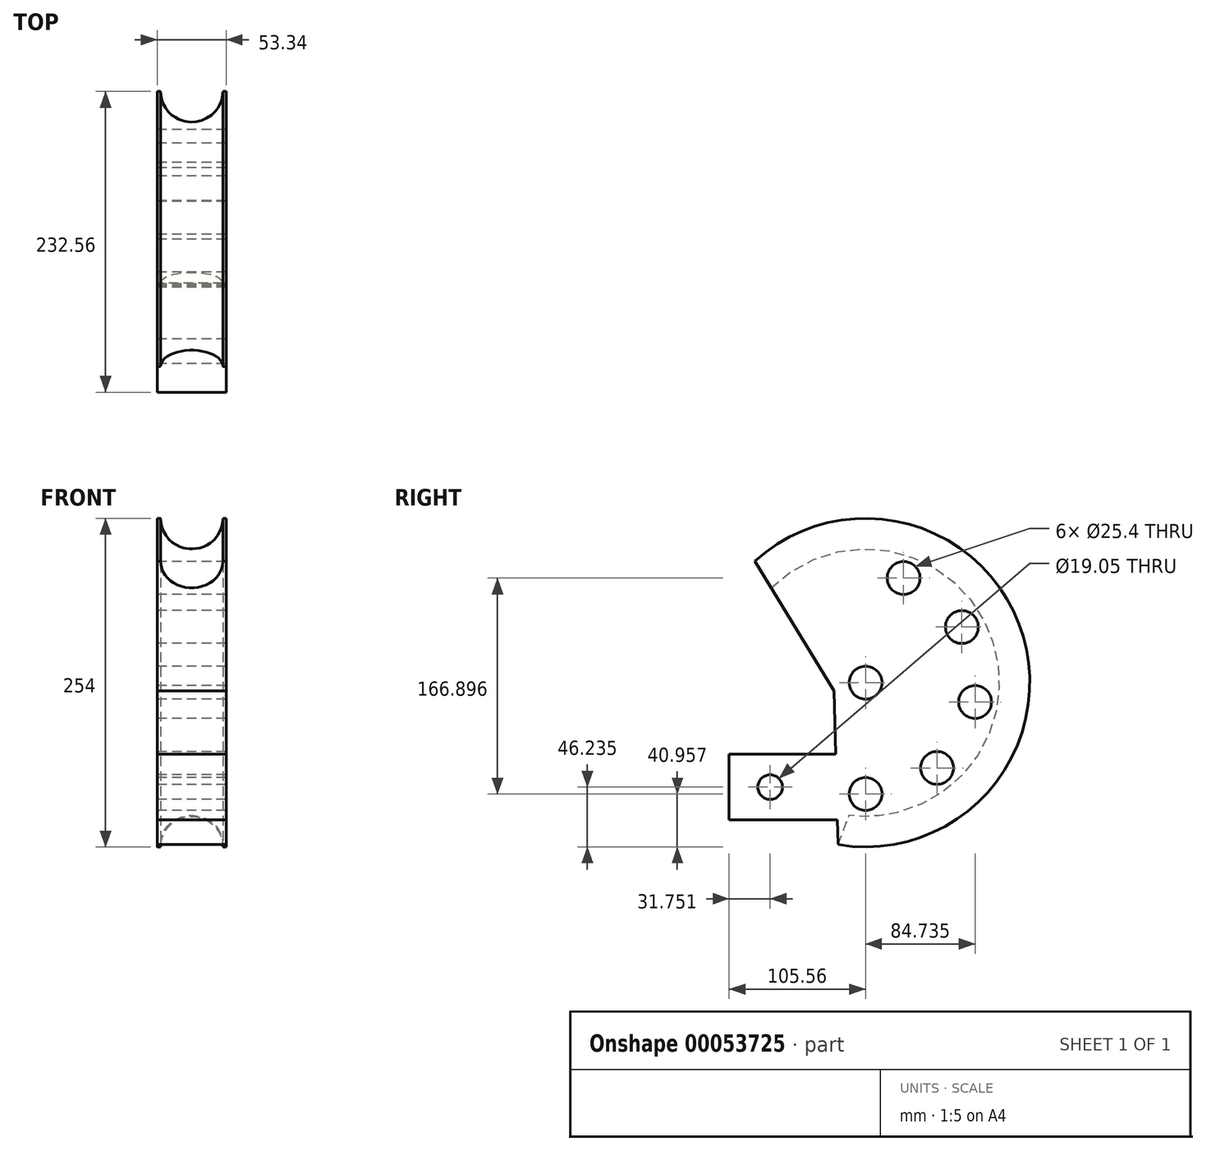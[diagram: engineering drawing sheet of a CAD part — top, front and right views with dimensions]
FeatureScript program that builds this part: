
annotation { "Feature Type Name" : "Feature", "Feature Type Description" : "" }
export const myFeature = defineFeature(function(context is Context, id is Id, definition is map)
    precondition{}
    {
        {
            var Q0;
            Q0=qCreatedBy(makeId("Right.planeOp"),FACE);
            var sketch = newSketch(context, id + "F0", { "sketchPlane" : qUnion([Q0])});
            skArc(sketch, "E0", {"start": v(-21.25, -125.2) * mm, "mid": v(121.85, 35.79) * mm, "end": v(-85.58, 93.83) * mm});
            skCircle(sketch, "E1", {"center": v(0, 0) * mm, "radius": 12.7 * mm});
            skCircle(sketch, "E2", {"center": v(0, -86.04) * mm, "radius": 12.7 * mm});
            skCircle(sketch, "E3.1.0", {"center": v(55.3, -65.91) * mm, "radius": 12.7 * mm});
            skCircle(sketch, "E3.2.0", {"center": v(84.74, -14.94) * mm, "radius": 12.7 * mm});
            skLineSegment(sketch, "E3.anchor1", {"start": v(0, 0) * mm, "end": v(0, -86.04) * mm, "construction": true});
            skLineSegment(sketch, "E3.anchor2", {"start": v(0, 0) * mm, "end": v(29.43, 80.85) * mm, "construction": true});
            skCircle(sketch, "E4.1.3.0", {"center": v(74.51, 43.02) * mm, "radius": 12.7 * mm});
            skCircle(sketch, "E4.1.4.0", {"center": v(29.43, 80.85) * mm, "radius": 12.7 * mm});
            skLineSegment(sketch, "E5.0", {"start": v(-24.24, -6.5) * mm, "end": v(-23, -55.37) * mm});
            skLineSegment(sketch, "E5.1", {"start": v(-24.24, -6.5) * mm, "end": v(-85.58, 93.83) * mm});
            skLineSegment(sketch, "E6", {"start": v(-21.73, -106.17) * mm, "end": v(-105.56, -106.17) * mm});
            skLineSegment(sketch, "E7", {"start": v(-105.56, -106.17) * mm, "end": v(-105.56, -55.37) * mm});
            skLineSegment(sketch, "E8", {"start": v(-105.56, -55.37) * mm, "end": v(-23, -55.37) * mm});
            skLineSegment(sketch, "E9.trimOffspring", {"start": v(-21.73, -106.17) * mm, "end": v(-21.25, -125.2) * mm});
            skCircle(sketch, "E10", {"center": v(-73.8, -80.77) * mm, "radius": 9.53 * mm});
            skPoint(sketch, "E10.centerSnap0", {"position": v(-105.56, -80.77) * mm});
            skSolve(sketch);
        }
        {
            var Q0;
            Q0=makeQuery(id+"F0.imprint","IMPRINT",FACE,{"disambiguationData":[TD([[makeQuery(id+"F0.imprint","IMPRINT",EDGE,{"derivedFrom":sQuery(id+"F0.wireOp",EDGE,"E0")}),1.0]])]});
            extrude(context, id + "F1", {"entities" : qUnion([Q0]), "depth" : 53.34 * mm});
        }
        {
            var Q0;
            Q0=makeQuery(id+"F1.opExtrude","SWEPT_FACE",FACE,{"disambiguationData":[OSD([sQuery(id+"F0.wireOp",EDGE,"E5.1")])]});
            var sketch = newSketch(context, id + "F2", { "sketchPlane" : qUnion([Q0])});
            skCircle(sketch, "E11", {"center": v(26.67, 124.7) * mm, "radius": 24.13 * mm});
            skSolve(sketch);
        }
        {
            var Q0;
            {var subQ0=sQuery(id+"F2.wireOp",EDGE,"E11");var subQ1=makeQuery(id+"F1.opExtrude","SWEPT_EDGE",EDGE,{"disambiguationData":[OSD([sQuery(id+"F0.wireOp",EDGE,"E0"),sQuery(id+"F0.wireOp",EDGE,"E5.1")])]});var subQ2=makeQuery(id+"F2.imprint","INTERSECT",VERTEX,{"disambiguationData":[OD(0.0)],"derivedFrom":[subQ1,subQ0]});Q0=makeQuery(id+"F2.imprint","IMPRINT",FACE,{"disambiguationData":[TD([[makeQuery(id+"F2.imprint","IMPRINT",EDGE,{"disambiguationData":[TD([[subQ2,1.0]])],"derivedFrom":subQ0}),1.0]])]});}
            var Q1;
            {var subQ0=sQuery(id+"F2.wireOp",EDGE,"E11");var subQ1=makeQuery(id+"F1.opExtrude","SWEPT_EDGE",EDGE,{"disambiguationData":[OSD([sQuery(id+"F0.wireOp",EDGE,"E0"),sQuery(id+"F0.wireOp",EDGE,"E5.1")])]});var subQ2=makeQuery(id+"F2.imprint","INTERSECT",VERTEX,{"disambiguationData":[OD(0.0)],"derivedFrom":[subQ1,subQ0]});Q1=makeQuery(id+"F2.imprint","IMPRINT",FACE,{"disambiguationData":[TD([[makeQuery(id+"F2.imprint","IMPRINT",EDGE,{"disambiguationData":[TD([[subQ2,-1.0]])],"derivedFrom":subQ0}),1.0]])]});}
            var Q2;
            Q2=makeQuery(id+"F1.opExtrude","CAP_EDGE",EDGE,{"disambiguationData":[OSD([sQuery(id+"F0.wireOp",EDGE,"E0")])],"isStart":false});
            sweep(context, id + "F3", {"operationType" : NewBodyOperationType.REMOVE, "profiles" : qUnion([Q0, Q1]), "path" : qUnion([Q2])});
        }
    });
